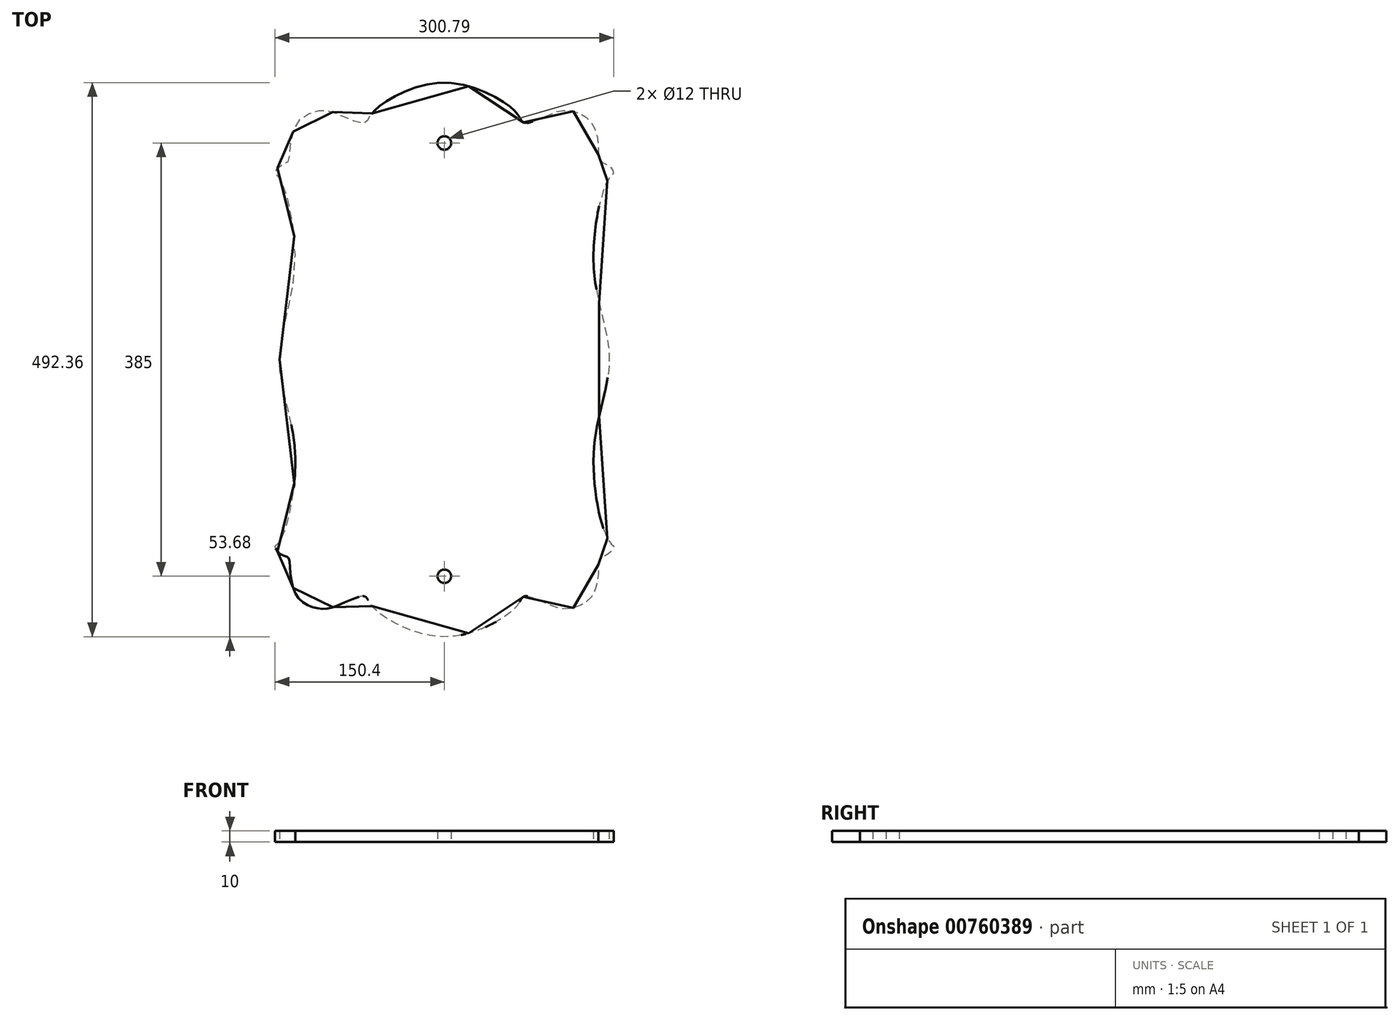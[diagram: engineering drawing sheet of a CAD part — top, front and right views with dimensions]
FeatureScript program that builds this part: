
annotation { "Feature Type Name" : "Feature", "Feature Type Description" : "" }
export const myFeature = defineFeature(function(context is Context, id is Id, definition is map)
    precondition{}
    {
        {
            var Q0;
            Q0=qCreatedBy(makeId("Top.planeOp"),FACE);
            var sketch = newSketch(context, id + "F0", { "sketchPlane" : qUnion([Q0])});
            skPoint(sketch, "E0", {"position": v(150.32, -165.76) * mm});
            skPoint(sketch, "E1", {"position": v(107.37, -221.56) * mm});
            skPoint(sketch, "E2", {"position": v(69.02, -211.72) * mm});
            skPoint(sketch, "E3", {"position": v(0, -246.18) * mm});
            skPoint(sketch, "E4", {"position": v(138.05, -177.25) * mm});
            skPoint(sketch, "E5", {"position": v(146.48, 0) * mm});
            skPoint(sketch, "E6", {"position": v(132.68, -82.88) * mm});
            skLineSegment(sketch, "E7", {"start": v(0, 292) * mm, "end": v(0, -246.18) * mm, "construction": true});
            skPoint(sketch, "E8.MirrorP", {"position": v(-146.48, 0) * mm});
            skPoint(sketch, "E9.MirrorP", {"position": v(-132.68, -82.88) * mm});
            skPoint(sketch, "E10.MirrorP", {"position": v(-150.32, -165.76) * mm});
            skPoint(sketch, "E11.MirrorP", {"position": v(-138.05, -177.25) * mm});
            skPoint(sketch, "E12.MirrorP", {"position": v(-107.37, -221.56) * mm});
            skPoint(sketch, "E13.MirrorP", {"position": v(-69.02, -211.72) * mm});
            skPoint(sketch, "E14", {"position": v(0, 0) * mm});
            skPoint(sketch, "E15", {"position": v(-146.25, -161.4) * mm});
            skPoint(sketch, "E16", {"position": v(-136.87, -189.28) * mm});
            skPoint(sketch, "E17", {"position": v(-146.26, -172.33) * mm});
            skPoint(sketch, "E18", {"position": v(-131.04, -210.06) * mm});
            skPoint(sketch, "E19", {"position": v(-94.82, -218.38) * mm});
            skPoint(sketch, "E20", {"position": v(-60.59, -222.84) * mm});
            skPoint(sketch, "E21", {"position": v(-67.25, -214.49) * mm});
            skPoint(sketch, "E22", {"position": v(-72.48, -210.2) * mm});
            skPoint(sketch, "E23", {"position": v(-119.37, -219.05) * mm});
            skPoint(sketch, "E24", {"position": v(-149.89, -167.68) * mm});
            skPoint(sketch, "E25.MirrorP", {"position": v(60.59, -222.84) * mm});
            skPoint(sketch, "E26.MirrorP", {"position": v(67.25, -214.49) * mm});
            skPoint(sketch, "E27.MirrorP", {"position": v(72.48, -210.2) * mm});
            skPoint(sketch, "E28.MirrorP", {"position": v(94.82, -218.38) * mm});
            skPoint(sketch, "E29.MirrorP", {"position": v(119.37, -219.05) * mm});
            skPoint(sketch, "E30.MirrorP", {"position": v(136.87, -189.28) * mm});
            skPoint(sketch, "E31.MirrorP", {"position": v(146.26, -172.33) * mm});
            skPoint(sketch, "E32.MirrorP", {"position": v(149.89, -167.68) * mm});
            skPoint(sketch, "E33.MirrorP", {"position": v(146.25, -161.4) * mm});
            skPoint(sketch, "E34", {"position": v(-139.73, -175.31) * mm});
            skPoint(sketch, "E35.MirrorP", {"position": v(131.04, -210.06) * mm});
            skPoint(sketch, "E36.MirrorP", {"position": v(-132.68, 82.88) * mm});
            skPoint(sketch, "E37.MirrorP", {"position": v(-139.73, 175.31) * mm});
            skPoint(sketch, "E38.MirrorP", {"position": v(-150.32, 165.76) * mm});
            skPoint(sketch, "E39.MirrorP", {"position": v(69.02, 211.72) * mm});
            skPoint(sketch, "E40.MirrorP", {"position": v(150.32, 165.76) * mm});
            skPoint(sketch, "E41.MirrorP", {"position": v(-67.25, 214.49) * mm});
            skPoint(sketch, "E42.MirrorP", {"position": v(131.04, 210.06) * mm});
            skPoint(sketch, "E43.MirrorP", {"position": v(60.59, 222.84) * mm});
            skPoint(sketch, "E44.MirrorP", {"position": v(119.37, 219.05) * mm});
            skPoint(sketch, "E45.MirrorP", {"position": v(136.87, 189.28) * mm});
            skPoint(sketch, "E46.MirrorP", {"position": v(-72.48, 210.2) * mm});
            skPoint(sketch, "E47.MirrorP", {"position": v(-138.05, 177.25) * mm});
            skPoint(sketch, "E48.MirrorP", {"position": v(-69.02, 211.72) * mm});
            skPoint(sketch, "E49.MirrorP", {"position": v(72.48, 210.2) * mm});
            skPoint(sketch, "E50.MirrorP", {"position": v(-146.25, 161.4) * mm});
            skPoint(sketch, "E51.MirrorP", {"position": v(-136.87, 189.28) * mm});
            skPoint(sketch, "E52.MirrorP", {"position": v(138.05, 177.25) * mm});
            skPoint(sketch, "E53.MirrorP", {"position": v(67.25, 214.49) * mm});
            skPoint(sketch, "E54.MirrorP", {"position": v(-149.89, 167.68) * mm});
            skPoint(sketch, "E55.MirrorP", {"position": v(149.89, 167.68) * mm});
            skPoint(sketch, "E56.MirrorP", {"position": v(-107.37, 221.56) * mm});
            skPoint(sketch, "E57.MirrorP", {"position": v(-94.82, 218.38) * mm});
            skPoint(sketch, "E58.MirrorP", {"position": v(146.26, 172.33) * mm});
            skPoint(sketch, "E59.MirrorP", {"position": v(107.37, 221.56) * mm});
            skPoint(sketch, "E60.MirrorP", {"position": v(-131.04, 210.06) * mm});
            skPoint(sketch, "E61.MirrorP", {"position": v(94.82, 218.38) * mm});
            skPoint(sketch, "E62.MirrorP", {"position": v(146.25, 161.4) * mm});
            skPoint(sketch, "E63.MirrorP", {"position": v(0, 246.18) * mm});
            skPoint(sketch, "E64.MirrorP", {"position": v(-146.26, 172.33) * mm});
            skPoint(sketch, "E65.MirrorP", {"position": v(-119.37, 219.05) * mm});
            skPoint(sketch, "E66.MirrorP", {"position": v(-60.59, 222.84) * mm});
            skPoint(sketch, "E67.MirrorP", {"position": v(132.68, 82.88) * mm});
            skFitSpline(sketch, "E68", {"points": [v(-146.48, 0) * mm, v(-132.68, 82.88) * mm, v(-146.25, 161.4) * mm, v(-150.32, 165.76) * mm, v(-149.89, 167.68) * mm, v(-146.26, 172.33) * mm, v(-139.73, 175.31) * mm, v(-138.05, 177.25) * mm, v(-136.87, 189.28) * mm, v(-131.04, 210.06) * mm, v(-119.37, 219.05) * mm, v(-107.37, 221.56) * mm, v(-94.82, 218.38) * mm, v(-72.48, 210.2) * mm, v(-69.02, 211.72) * mm, v(-67.25, 214.49) * mm, v(-60.59, 222.84) * mm, v(0, 246.18) * mm, v(60.59, 222.84) * mm, v(67.25, 214.49) * mm, v(69.02, 211.72) * mm, v(72.48, 210.2) * mm, v(94.82, 218.38) * mm, v(107.37, 221.56) * mm, v(119.37, 219.05) * mm, v(131.04, 210.06) * mm, v(136.87, 189.28) * mm, v(138.05, 177.25) * mm, v(146.26, 172.33) * mm, v(149.89, 167.68) * mm, v(150.32, 165.76) * mm, v(146.25, 161.4) * mm, v(132.68, 82.88) * mm, v(146.48, 0) * mm, v(132.68, -82.88) * mm, v(146.25, -161.4) * mm, v(150.32, -165.76) * mm, v(149.89, -167.68) * mm, v(146.26, -172.33) * mm, v(138.05, -177.25) * mm, v(136.87, -189.28) * mm, v(131.04, -210.06) * mm, v(119.37, -219.05) * mm, v(107.37, -221.56) * mm, v(94.82, -218.38) * mm, v(72.48, -210.2) * mm, v(69.02, -211.72) * mm, v(67.25, -214.49) * mm, v(60.59, -222.84) * mm, v(0, -246.18) * mm, v(-60.59, -222.84) * mm, v(-67.25, -214.49) * mm, v(-69.02, -211.72) * mm, v(-72.48, -210.2) * mm, v(-94.82, -218.38) * mm, v(-107.37, -221.56) * mm, v(-119.37, -219.05) * mm, v(-131.04, -210.06) * mm, v(-136.87, -189.28) * mm, v(-138.05, -177.25) * mm, v(-139.73, -175.31) * mm, v(-146.26, -172.33) * mm, v(-149.89, -167.68) * mm, v(-150.32, -165.76) * mm, v(-146.25, -161.4) * mm, v(-132.68, -82.88) * mm, v(-146.48, 0) * mm]});
            skPoint(sketch, "E69", {"position": v(0, 295) * mm});
            skPoint(sketch, "E70", {"position": v(-30, 295) * mm});
            skPoint(sketch, "E71", {"position": v(-225, 0) * mm});
            skPoint(sketch, "E72", {"position": v(-225, 100) * mm});
            skPoint(sketch, "E73.MirrorP", {"position": v(225, 100) * mm});
            skPoint(sketch, "E74.MirrorP", {"position": v(225, -60) * mm});
            skLineSegment(sketch, "E75", {"start": v(0, 0) * mm, "end": v(-373.3, 215.53) * mm, "construction": true});
            skLineSegment(sketch, "E76", {"start": v(0, 0) * mm, "end": v(-204.64, 354.44) * mm, "construction": true});
            skLineSegment(sketch, "E77", {"start": v(-225, 0) * mm, "end": v(-225, 100) * mm});
            skLineSegment(sketch, "E78", {"start": v(-30, 295) * mm, "end": v(0, 295) * mm});
            skPoint(sketch, "E79", {"position": v(-30, 100) * mm});
            skArc(sketch, "E80", {"start": v(-30, 295) * mm, "mid": v(-167.89, 237.89) * mm, "end": v(-225, 100) * mm});
            skLineSegment(sketch, "E81.MirrorCS", {"start": v(225, 0) * mm, "end": v(225, 100) * mm});
            skArc(sketch, "E82.MirrorCS", {"start": v(30, 295) * mm, "mid": v(167.89, 237.89) * mm, "end": v(225, 100) * mm});
            skLineSegment(sketch, "E83.MirrorCS", {"start": v(30, 295) * mm, "end": v(0, 295) * mm});
            skArc(sketch, "E84.MirrorCS", {"start": v(-30, -295) * mm, "mid": v(-167.89, -237.89) * mm, "end": v(-225, -100) * mm});
            skLineSegment(sketch, "E85.MirrorCS", {"start": v(-225, 0) * mm, "end": v(-225, -100) * mm});
            skLineSegment(sketch, "E86.MirrorCS", {"start": v(225, 0) * mm, "end": v(225, -100) * mm});
            skArc(sketch, "E87.MirrorCS", {"start": v(30, -295) * mm, "mid": v(167.89, -237.89) * mm, "end": v(225, -100) * mm});
            skLineSegment(sketch, "E88.MirrorCS", {"start": v(30, -295) * mm, "end": v(0, -295) * mm});
            skLineSegment(sketch, "E89.MirrorCS", {"start": v(-30, -295) * mm, "end": v(0, -295) * mm});
            skCircle(sketch, "E90", {"center": v(0, 192.5) * mm, "radius": 6 * mm});
            skCircle(sketch, "E91.MirrorC", {"center": v(0, -192.5) * mm, "radius": 6 * mm});
            skSolve(sketch);
        }
        {
            var Q0;
            Q0=makeQuery(id+"F0.imprint","IMPRINT",FACE,{"disambiguationData":[TD([[makeQuery(id+"F0.imprint","IMPRINT",EDGE,{"derivedFrom":sQuery(id+"F0.wireOp",EDGE,"E68")}),-1.0]])]});
            extrude(context, id + "F1", {"entities" : qUnion([Q0]), "endBound" : BoundingType.SYMMETRIC, "depth" : 10 * mm});
        }
        {
            var Q0;
            Q0=makeQuery(id+"F1.opExtrude","CAP_FACE",FACE,{"disambiguationData":[OSD([sQuery(id+"F0.wireOp",EDGE,"E68"),sQuery(id+"F0.wireOp",EDGE,"E90"),sQuery(id+"F0.wireOp",EDGE,"E91.MirrorC")])],"isStart":false});
            cPlane(context, id + "F2", {"entities" : qUnion([Q0]), "cplaneType" : CPlaneType.OFFSET, "offset" : 50 * mm, "width" : 150 * mm, "height" : 150 * mm});
        }
    });
